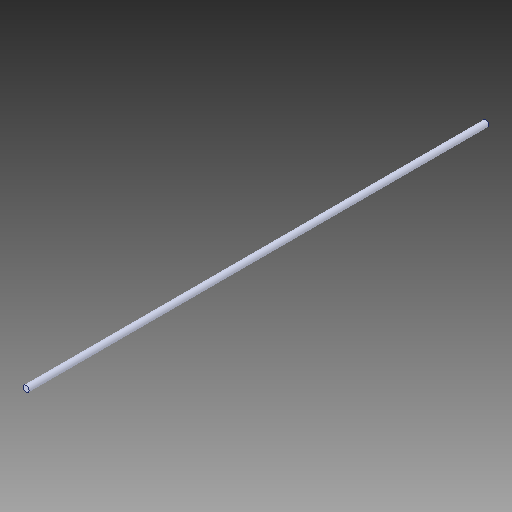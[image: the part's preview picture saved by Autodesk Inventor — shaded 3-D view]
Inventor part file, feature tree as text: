
AUTODESK INVENTOR PART (.ipt)
format: ipt  version: 2018 (Build 220112000, 112)  size: 78,336 bytes
history: native  units: in
note: dims shown in document units (in); Inventor stores cm internally (conversion verified against a paired STEP export)
features: sketch x1, other x1
ambient origin geometry x8: Origin, YZ Plane, XZ Plane, XY Plane, X Axis, Y Axis, Z Axis, Center Point
bodies: Solid1 (feature_tree)
feature tree (2):
  sketch  "Sketch1"
  other  "Boss-Extrude1"
